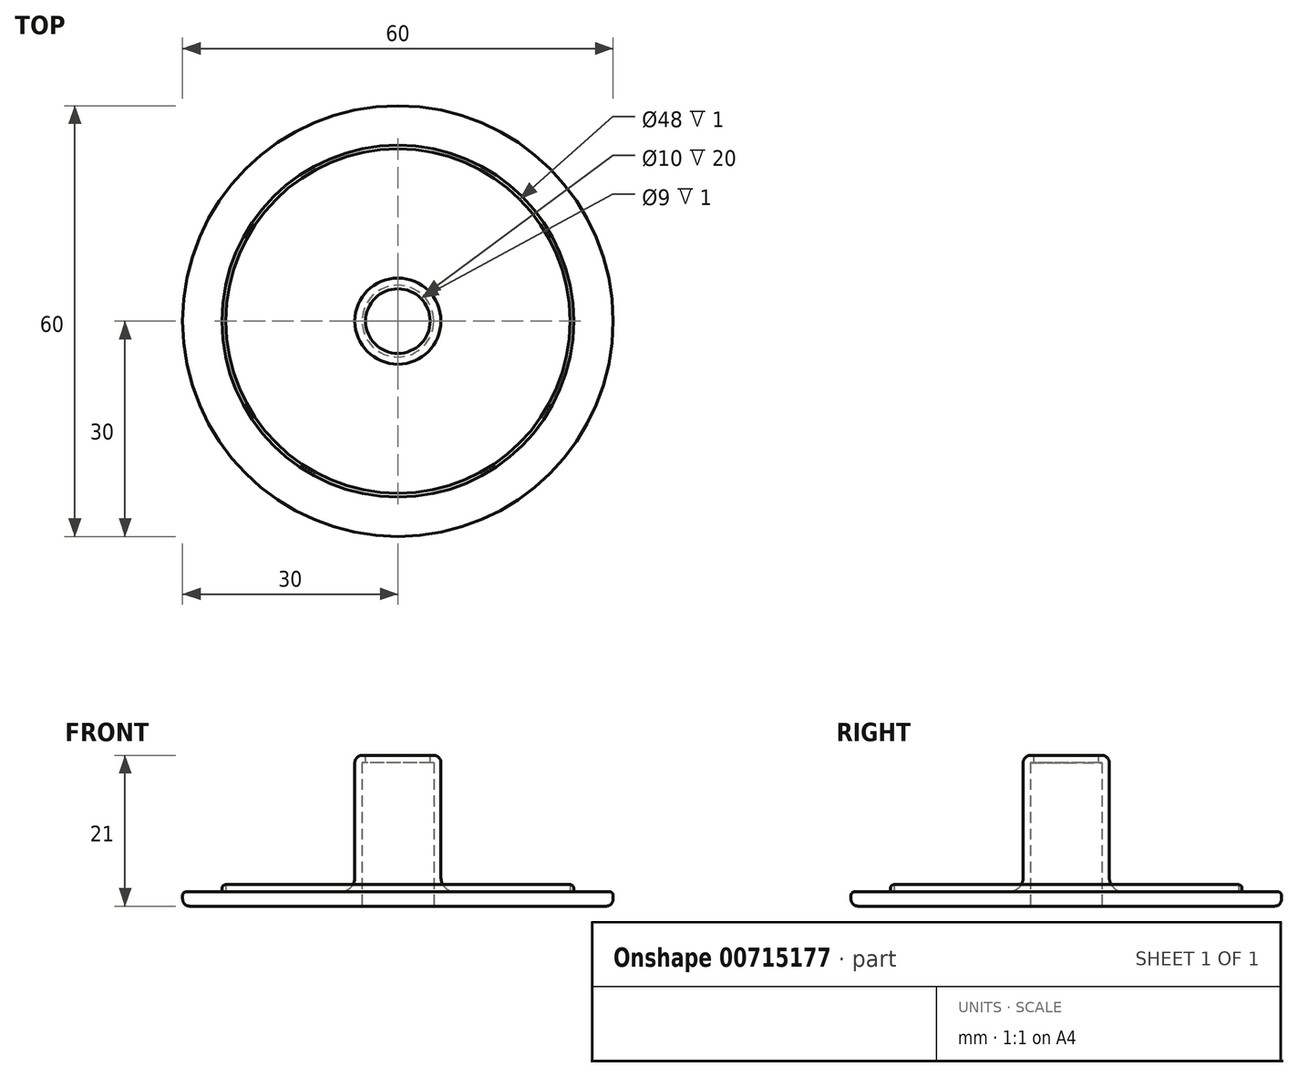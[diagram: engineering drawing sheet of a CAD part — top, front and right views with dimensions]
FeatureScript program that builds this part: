
annotation { "Feature Type Name" : "Feature", "Feature Type Description" : "" }
export const myFeature = defineFeature(function(context is Context, id is Id, definition is map)
    precondition{}
    {
        {
            var Q0;
            Q0=qCreatedBy(makeId("Top.planeOp"),FACE);
            var sketch = newSketch(context, id + "F0", { "sketchPlane" : qUnion([Q0])});
            skCircle(sketch, "E0", {"center": v(0, 0) * mm, "radius": 30 * mm});
            skSolve(sketch);
        }
        {
            var Q0;
            Q0 = qSketchRegion(id + "F0", true);
            extrude(context, id + "F1", {"entities" : qUnion([Q0]), "depth" : 2 * mm, "offsetDistance" : 25 * mm});
        }
        {
            var Q0;
            Q0=qCreatedBy(makeId("Top.planeOp"),FACE);
            var sketch = newSketch(context, id + "F2", { "sketchPlane" : qUnion([Q0])});
            skCircle(sketch, "E1", {"center": v(0, 0) * mm, "radius": 24.5 * mm});
            skCircle(sketch, "E2", {"center": v(0, 0) * mm, "radius": 24 * mm});
            skSolve(sketch);
        }
        {
            var Q0;
            Q0=makeQuery(id+"F2.imprint","IMPRINT",FACE,{"disambiguationData":[TD([[makeQuery(id+"F2.imprint","IMPRINT",EDGE,{"derivedFrom":sQuery(id+"F2.wireOp",EDGE,"E1")}),1.0]])]});
            extrude(context, id + "F3", {"entities" : qUnion([Q0]), "operationType" : NewBodyOperationType.ADD, "depth" : 3 * mm, "offsetDistance" : 25 * mm});
        }
        {
            var Q0;
            Q0=qCreatedBy(makeId("Top.planeOp"),FACE);
            var sketch = newSketch(context, id + "F4", { "sketchPlane" : qUnion([Q0])});
            skCircle(sketch, "E3", {"center": v(0, 0) * mm, "radius": 6 * mm});
            skSolve(sketch);
        }
        {
            var Q0;
            Q0 = qSketchRegion(id + "F4", true);
            extrude(context, id + "F5", {"entities" : qUnion([Q0]), "operationType" : NewBodyOperationType.ADD, "depth" : 21 * mm, "offsetDistance" : 25 * mm});
        }
        {
            var Q0;
            Q0=qCreatedBy(makeId("Top.planeOp"),FACE);
            var sketch = newSketch(context, id + "F6", { "sketchPlane" : qUnion([Q0])});
            skCircle(sketch, "E4", {"center": v(0, 0) * mm, "radius": 5 * mm});
            skSolve(sketch);
        }
        {
            var Q0;
            Q0=makeQuery(id+"F6.imprint","IMPRINT",FACE,{"disambiguationData":[TD([[makeQuery(id+"F6.imprint","IMPRINT",EDGE,{"derivedFrom":sQuery(id+"F6.wireOp",EDGE,"E4")}),1.0]])]});
            var Q1;
            Q1=sQuery(id+"F6.wireOp",EDGE,"E4");
            extrude(context, id + "F7", {"entities" : qUnion([Q0]), "operationType" : NewBodyOperationType.REMOVE, "surfaceEntities" : qUnion([Q1]), "oppositeDirection" : true, "depth" : 0 * mm, "offsetDistance" : 25 * mm, "hasSecondDirection" : true, "secondDirectionOppositeDirection" : false, "secondDirectionDepth" : 20 * mm});
        }
        {
            var Q0;
            Q0=qCreatedBy(makeId("Top.planeOp"),FACE);
            var sketch = newSketch(context, id + "F8", { "sketchPlane" : qUnion([Q0])});
            skCircle(sketch, "E5", {"center": v(0, 0) * mm, "radius": 4.5 * mm});
            skSolve(sketch);
        }
        {
            var Q0;
            Q0=makeQuery(id+"F8.imprint","IMPRINT",FACE,{"disambiguationData":[TD([[makeQuery(id+"F8.imprint","IMPRINT",EDGE,{"derivedFrom":sQuery(id+"F8.wireOp",EDGE,"E5")}),1.0]])]});
            var Q1;
            Q1=sQuery(id+"F8.wireOp",EDGE,"E5");
            extrude(context, id + "F9", {"entities" : qUnion([Q0]), "operationType" : NewBodyOperationType.REMOVE, "surfaceEntities" : qUnion([Q1]), "oppositeDirection" : true, "depth" : 25 * mm, "offsetDistance" : 25 * mm, "hasSecondDirection" : true, "secondDirectionOppositeDirection" : false, "secondDirectionDepth" : 25 * mm});
        }
        {
            var Q0;
            Q0=makeQuery(id+"F1.opExtrude","CAP_EDGE",EDGE,{"disambiguationData":[OSD([sQuery(id+"F0.wireOp",EDGE,"E0")])],"isStart":true});
            var Q1;
            Q1=makeQuery(id+"F7.boolean.opBoolean","COPY",EDGE,{"derivedFrom":makeQuery(id+"F7.opExtrude","CAP_EDGE",EDGE,{"disambiguationData":[OSD([sQuery(id+"F6.wireOp",EDGE,"E4")])],"isStart":false})});
            var Q2;
            Q2=makeQuery(id+"F5.opExtrude","CAP_EDGE",EDGE,{"disambiguationData":[OSD([sQuery(id+"F4.wireOp",EDGE,"E3")])],"isStart":false});
            fillet(context, id + "F10", {"entities" : qUnion([Q0, Q1, Q2]), "radius" : 1 * mm, "tangentPropagation" : true, "allowEdgeOverflow" : false});
        }
        {
            var Q0;
            Q0=makeQuery(id+"F3.opExtrude","CAP_EDGE",EDGE,{"disambiguationData":[OSD([sQuery(id+"F2.wireOp",EDGE,"E1")])],"isStart":false});
            var Q1;
            Q1=makeQuery(id+"F1.opExtrude","CAP_EDGE",EDGE,{"disambiguationData":[OSD([sQuery(id+"F0.wireOp",EDGE,"E0")])],"isStart":false});
            fillet(context, id + "F11", {"entities" : qUnion([Q0, Q1]), "radius" : 0.5 * mm, "tangentPropagation" : true, "allowEdgeOverflow" : false});
        }
        {
            var Q0;
            Q0=makeQuery(id+"F5.boolean.opBoolean","INTERSECT",EDGE,{"derivedFrom":[makeQuery(id+"F3.boolean.opBoolean","SPLIT",FACE,{"disambiguationData":[TD([makeQuery(id+"F3.opExtrude","SWEPT_FACE",FACE,{"disambiguationData":[OSD([sQuery(id+"F2.wireOp",EDGE,"E2")])]})])],"derivedFrom":makeQuery(id+"F1.opExtrude","CAP_FACE",FACE,{"disambiguationData":[OSD([sQuery(id+"F0.wireOp",EDGE,"E0")])],"isStart":false})}),makeQuery(id+"F5.opExtrude","SWEPT_FACE",FACE,{"disambiguationData":[OSD([sQuery(id+"F4.wireOp",EDGE,"E3")])]})]});
            fillet(context, id + "F12", {"entities" : qUnion([Q0]), "radius" : 2 * mm, "tangentPropagation" : true, "allowEdgeOverflow" : false});
        }
    });
